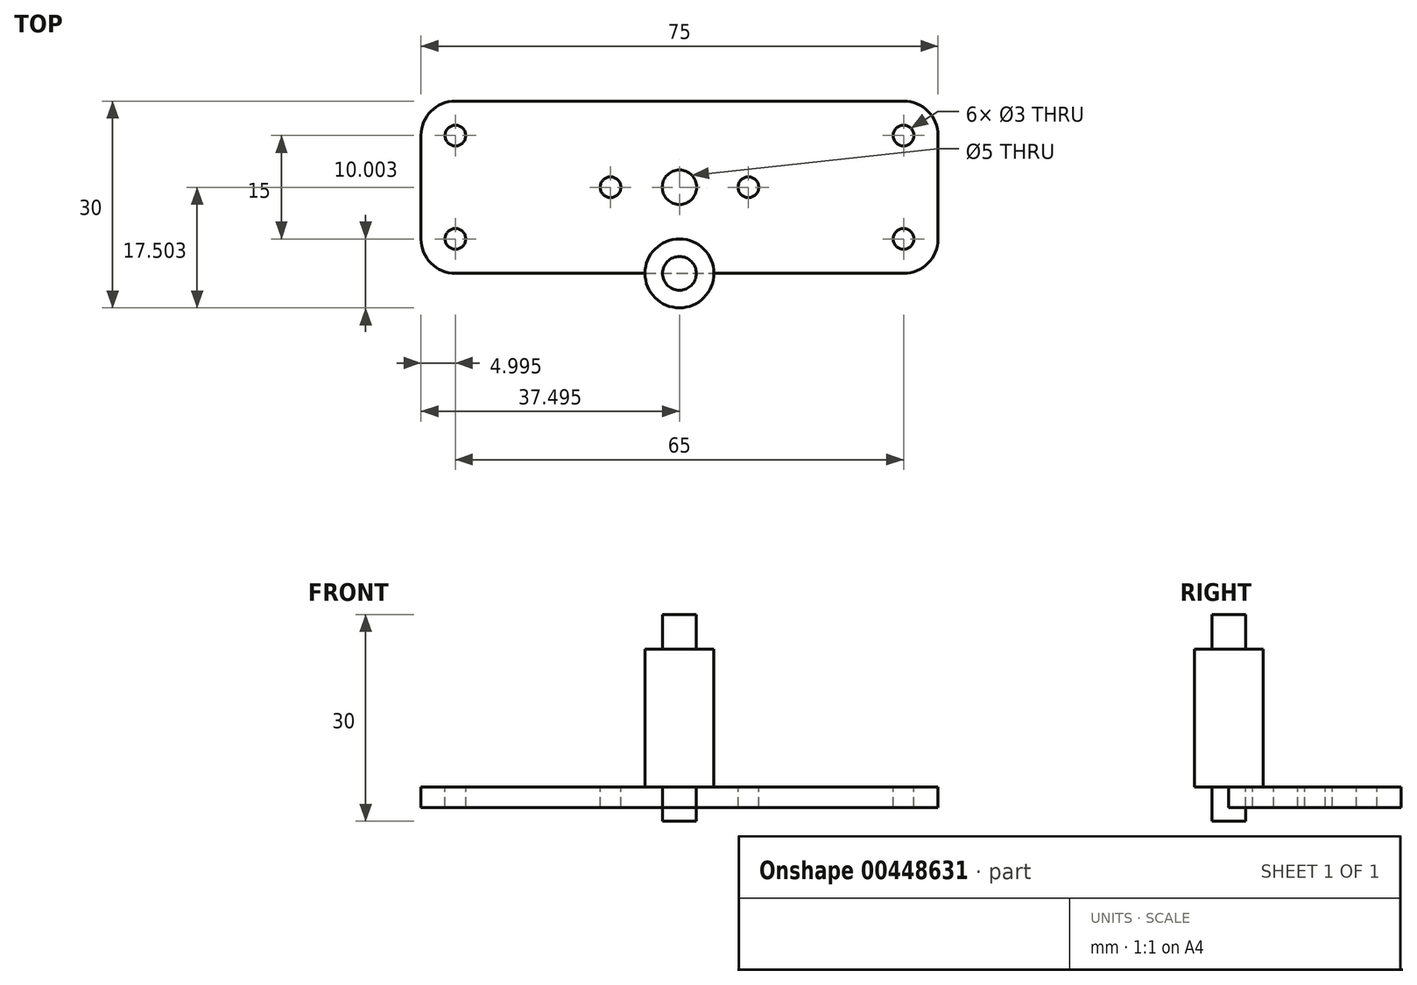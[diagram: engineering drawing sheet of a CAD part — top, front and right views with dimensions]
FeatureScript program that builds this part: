
annotation { "Feature Type Name" : "Feature", "Feature Type Description" : "" }
export const myFeature = defineFeature(function(context is Context, id is Id, definition is map)
    precondition{}
    {
        {
            var Q0;
            Q0=qCreatedBy(makeId("Top.planeOp"),FACE);
            var sketch = newSketch(context, id + "F0", { "sketchPlane" : qUnion([Q0])});
            skLineSegment(sketch, "E0.bottom", {"start": v(-34.57, -39.05) * mm, "end": v(30.43, -39.05) * mm});
            skLineSegment(sketch, "E0.top", {"start": v(-34.57, -14.05) * mm, "end": v(30.43, -14.05) * mm});
            skLineSegment(sketch, "E0.left", {"start": v(-39.57, -34.05) * mm, "end": v(-39.57, -19.05) * mm});
            skLineSegment(sketch, "E0.right", {"start": v(35.43, -34.05) * mm, "end": v(35.43, -19.05) * mm});
            skPoint(sketch, "E1.visualSharp", {"position": v(35.43, -14.05) * mm});
            skArc(sketch, "E1.filletArc", {"start": v(35.43, -19.05) * mm, "mid": v(33.96, -15.51) * mm, "end": v(30.43, -14.05) * mm});
            skPoint(sketch, "E2.visualSharp", {"position": v(-39.57, -39.05) * mm});
            skArc(sketch, "E2.filletArc", {"start": v(-39.57, -34.05) * mm, "mid": v(-38.11, -37.58) * mm, "end": v(-34.57, -39.05) * mm});
            skPoint(sketch, "E3.visualSharp", {"position": v(-39.57, -14.05) * mm});
            skArc(sketch, "E3.filletArc", {"start": v(-34.57, -14.05) * mm, "mid": v(-38.11, -15.51) * mm, "end": v(-39.57, -19.05) * mm});
            skPoint(sketch, "E4.visualSharp", {"position": v(35.43, -39.05) * mm});
            skArc(sketch, "E4.filletArc", {"start": v(30.43, -39.05) * mm, "mid": v(33.96, -37.58) * mm, "end": v(35.43, -34.05) * mm});
            skSolve(sketch);
        }
        {
            var Q0;
            Q0=makeQuery(id+"F0.imprint","IMPRINT",FACE,{"disambiguationData":[TD([[makeQuery(id+"F0.imprint","IMPRINT",EDGE,{"derivedFrom":sQuery(id+"F0.wireOp",EDGE,"E0.bottom")}),1.0]])]});
            extrude(context, id + "F1", {"entities" : qUnion([Q0]), "depth" : 3 * mm});
        }
        {
            var Q0;
            Q0=makeQuery(id+"F1.opExtrude","CAP_FACE",FACE,{"disambiguationData":[OSD([sQuery(id+"F0.wireOp",EDGE,"E0.bottom"),sQuery(id+"F0.wireOp",EDGE,"E0.top"),sQuery(id+"F0.wireOp",EDGE,"E0.left"),sQuery(id+"F0.wireOp",EDGE,"E0.right"),sQuery(id+"F0.wireOp",EDGE,"E1.filletArc"),sQuery(id+"F0.wireOp",EDGE,"E2.filletArc"),sQuery(id+"F0.wireOp",EDGE,"E3.filletArc"),sQuery(id+"F0.wireOp",EDGE,"E4.filletArc")])],"isStart":false});
            var sketch = newSketch(context, id + "F2", { "sketchPlane" : qUnion([Q0])});
            skCircle(sketch, "E5", {"center": v(-34.57, -19.05) * mm, "radius": 1.5 * mm});
            skCircle(sketch, "E6", {"center": v(-34.57, -34.05) * mm, "radius": 1.5 * mm});
            skCircle(sketch, "E7", {"center": v(30.43, -19.05) * mm, "radius": 1.5 * mm});
            skCircle(sketch, "E8", {"center": v(30.43, -34.05) * mm, "radius": 1.5 * mm});
            skCircle(sketch, "E9", {"center": v(-2.07, -26.55) * mm, "radius": 2.5 * mm});
            skPoint(sketch, "E9.centerSnap0", {"position": v(-2.07, -14.05) * mm});
            skPoint(sketch, "E9.centerSnap1", {"position": v(-39.57, -26.55) * mm});
            skCircle(sketch, "E10", {"center": v(-12.07, -26.55) * mm, "radius": 1.5 * mm});
            skCircle(sketch, "E11", {"center": v(7.93, -26.55) * mm, "radius": 1.5 * mm});
            skSolve(sketch);
        }
        {
            var Q0;
            Q0 = qSketchRegion(id + "F2", true);
            var Q1;
            Q1=makeQuery(id+"F1.opExtrude","CAP_FACE",FACE,{"disambiguationData":[OSD([sQuery(id+"F0.wireOp",EDGE,"E0.bottom"),sQuery(id+"F0.wireOp",EDGE,"E0.top"),sQuery(id+"F0.wireOp",EDGE,"E0.left"),sQuery(id+"F0.wireOp",EDGE,"E0.right"),sQuery(id+"F0.wireOp",EDGE,"E1.filletArc"),sQuery(id+"F0.wireOp",EDGE,"E2.filletArc"),sQuery(id+"F0.wireOp",EDGE,"E3.filletArc"),sQuery(id+"F0.wireOp",EDGE,"E4.filletArc")])],"isStart":true});
            extrude(context, id + "F3", {"entities" : qUnion([Q0]), "operationType" : NewBodyOperationType.REMOVE, "endBound" : BoundingType.UP_TO_SURFACE, "oppositeDirection" : true, "endBoundEntityFace" : qUnion([Q1]), "depth" : 5 * mm});
        }
        {
            var Q0;
            Q0=makeQuery(id+"F1.opExtrude","SWEPT_FACE",FACE,{"disambiguationData":[OSD([sQuery(id+"F0.wireOp",EDGE,"E0.bottom")])]});
            var sketch = newSketch(context, id + "F4", { "sketchPlane" : qUnion([Q0])});
            skLineSegment(sketch, "E12", {"start": v(-2.07, 3) * mm, "end": v(-2.07, -2) * mm});
            skLineSegment(sketch, "E13", {"start": v(-2.07, -2) * mm, "end": v(-4.52, -2) * mm});
            skLineSegment(sketch, "E14", {"start": v(-4.52, -2) * mm, "end": v(-4.52, 3) * mm});
            skLineSegment(sketch, "E15", {"start": v(-4.52, 3) * mm, "end": v(-7.07, 3) * mm});
            skLineSegment(sketch, "E16", {"start": v(-7.07, 3) * mm, "end": v(-7.07, 23) * mm});
            skLineSegment(sketch, "E17", {"start": v(-7.07, 23) * mm, "end": v(-4.52, 23) * mm});
            skLineSegment(sketch, "E18", {"start": v(-4.52, 23) * mm, "end": v(-4.52, 28) * mm});
            skLineSegment(sketch, "E19", {"start": v(-4.52, 28) * mm, "end": v(-2.07, 28) * mm});
            skLineSegment(sketch, "E20", {"start": v(-2.07, 28) * mm, "end": v(-2.07, 3) * mm});
            skSolve(sketch);
        }
        {
            var Q0;
            {var subQ2=sQuery(id+"F4.wireOp",EDGE,"E15");Q0=makeQuery(id+"F4.imprint","IMPRINT",FACE,{"disambiguationData":[TD([[makeQuery(id+"F4.imprint","IMPRINT",EDGE,{"derivedFrom":subQ2}),1.0]])]});}
            var Q1;
            {var subQ0=sQuery(id+"F4.wireOp",EDGE,"E13");Q1=makeQuery(id+"F4.imprint","IMPRINT",FACE,{"disambiguationData":[TD([[makeQuery(id+"F4.imprint","IMPRINT",EDGE,{"derivedFrom":subQ0}),-1.0]])]});}
            var Q2;
            {var subQ0=sQuery(id+"F4.wireOp",EDGE,"E12");var subQ1=sQuery(id+"F0.wireOp",EDGE,"E0.bottom");var subQ4=makeQuery(id+"F1.opExtrude","CAP_EDGE",EDGE,{"disambiguationData":[OSD([subQ1])],"isStart":true});var subQ5=makeQuery(id+"F4.imprint","INTERSECT",VERTEX,{"derivedFrom":[subQ4,subQ0]});Q2=makeQuery(id+"F4.imprint","IMPRINT",FACE,{"disambiguationData":[TD([[makeQuery(id+"F4.imprint","IMPRINT",EDGE,{"disambiguationData":[TD([[subQ5,1.0]])],"derivedFrom":subQ4}),1.0]])]});}
            var Q3;
            Q3=sQuery(id+"F4.wireOp",EDGE,"E20");
            revolve(context, id + "F5", {"entities" : qUnion([Q0, Q1, Q2]), "axis" : qUnion([Q3]), "revolveType" : RevolveType.FULL});
        }
    });
